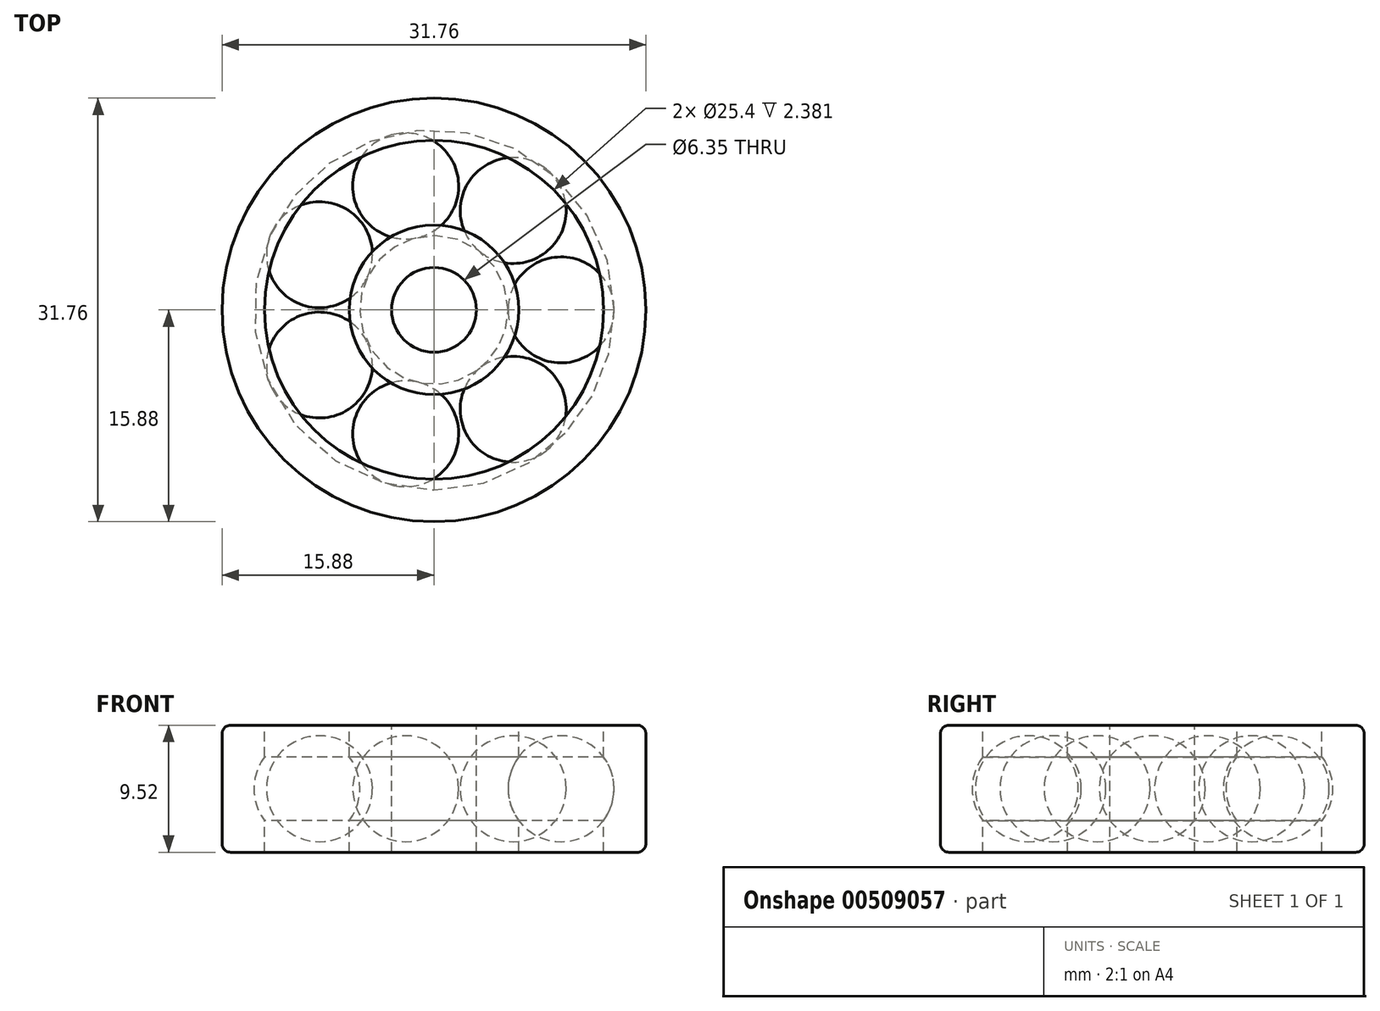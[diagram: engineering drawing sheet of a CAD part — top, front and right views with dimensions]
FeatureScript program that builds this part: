
annotation { "Feature Type Name" : "Feature", "Feature Type Description" : "" }
export const myFeature = defineFeature(function(context is Context, id is Id, definition is map)
    precondition{}
    {
        {
            var Q0;
            Q0=qCreatedBy(makeId("Front.planeOp"),FACE);
            var sketch = newSketch(context, id + "F0", { "sketchPlane" : qUnion([Q0])});
            skLineSegment(sketch, "E0", {"start": v(0, 19.05) * mm, "end": v(0, -19.05) * mm, "construction": true});
            skLineSegment(sketch, "E1", {"start": v(12.7, 19.05) * mm, "end": v(12.7, -19.05) * mm});
            skLineSegment(sketch, "E2", {"start": v(12.7, -19.05) * mm, "end": v(25.4, -19.05) * mm});
            skLineSegment(sketch, "E3", {"start": v(25.4, -19.05) * mm, "end": v(25.4, 19.05) * mm});
            skLineSegment(sketch, "E4", {"start": v(25.4, 19.05) * mm, "end": v(12.7, 19.05) * mm});
            skCircle(sketch, "E5", {"center": v(38.1, 0) * mm, "radius": 15.88 * mm});
            skLineSegment(sketch, "E6.bottom", {"start": v(50.8, 19.05) * mm, "end": v(63.5, 19.05) * mm});
            skLineSegment(sketch, "E6.top", {"start": v(50.8, -19.05) * mm, "end": v(63.5, -19.05) * mm});
            skLineSegment(sketch, "E6.left", {"start": v(50.8, 19.05) * mm, "end": v(50.8, -19.05) * mm});
            skLineSegment(sketch, "E6.right", {"start": v(63.5, 19.05) * mm, "end": v(63.5, -19.05) * mm});
            skLineSegment(sketch, "E7", {"start": v(22.22, 0) * mm, "end": v(53.97, 0) * mm});
            skLineSegment(sketch, "E8", {"start": v(12.7, 0) * mm, "end": v(22.22, 0) * mm, "construction": true});
            skLineSegment(sketch, "E9", {"start": v(53.97, 0) * mm, "end": v(63.5, 0) * mm, "construction": true});
            skSolve(sketch);
        }
        {
            var Q0;
            {var subQ0=sQuery(id+"F0.wireOp",EDGE,"E5");var subQ1=sQuery(id+"F0.wireOp",EDGE,"E3");var subQ2=makeQuery(id+"F0.imprint","INTERSECT",VERTEX,{"disambiguationData":[OD(1.0)],"derivedFrom":[subQ1,subQ0]});Q0=makeQuery(id+"F0.imprint","IMPRINT",FACE,{"disambiguationData":[TD([[makeQuery(id+"F0.imprint","IMPRINT",EDGE,{"disambiguationData":[TD([[subQ2,1.0]])],"derivedFrom":subQ1}),-1.0]])]});}
            var Q1;
            {var subQ0=sQuery(id+"F0.wireOp",EDGE,"E5");var subQ1=sQuery(id+"F0.wireOp",EDGE,"E3");var subQ2=makeQuery(id+"F0.imprint","INTERSECT",VERTEX,{"disambiguationData":[OD(1.0)],"derivedFrom":[subQ1,subQ0]});Q1=makeQuery(id+"F0.imprint","IMPRINT",FACE,{"disambiguationData":[TD([[makeQuery(id+"F0.imprint","IMPRINT",EDGE,{"disambiguationData":[TD([[subQ2,1.0]])],"derivedFrom":subQ1}),1.0]])]});}
            var Q2;
            {var subQ0=sQuery(id+"F0.wireOp",EDGE,"E7");var subQ1=sQuery(id+"F0.wireOp",EDGE,"E5");var subQ2=makeQuery(id+"F0.imprint","INTERSECT",VERTEX,{"disambiguationData":[OD(1.0)],"derivedFrom":[subQ1,subQ0]});Q2=makeQuery(id+"F0.imprint","IMPRINT",FACE,{"disambiguationData":[TD([[makeQuery(id+"F0.imprint","IMPRINT",EDGE,{"disambiguationData":[TD([[subQ2,-1.0]])],"derivedFrom":subQ1}),1.0]])]});}
            var Q3;
            Q3=sQuery(id+"F0.wireOp",EDGE,"E7");
            revolve(context, id + "F1", {"entities" : qUnion([Q0, Q1, Q2]), "axis" : qUnion([Q3]), "revolveType" : RevolveType.FULL});
        }
        {
            var Q0;
            Q0=makeQuery(id+"F0.imprint","IMPRINT",FACE,{"disambiguationData":[TD([[makeQuery(id+"F0.imprint","IMPRINT",EDGE,{"derivedFrom":sQuery(id+"F0.wireOp",EDGE,"E1")}),1.0]])]});
            var Q1;
            Q1=sQuery(id+"F0.wireOp",EDGE,"E0");
            revolve(context, id + "F2", {"entities" : qUnion([Q0]), "axis" : qUnion([Q1]), "revolveType" : RevolveType.FULL});
        }
        {
            var Q0;
            {var subQ1=sQuery(id+"F0.wireOp",EDGE,"E6.bottom");Q0=makeQuery(id+"F0.imprint","IMPRINT",FACE,{"disambiguationData":[TD([[makeQuery(id+"F0.imprint","IMPRINT",EDGE,{"derivedFrom":subQ1}),-1.0]])]});}
            var Q1;
            Q1=sQuery(id+"F0.wireOp",EDGE,"E0");
            revolve(context, id + "F3", {"entities" : qUnion([Q0]), "axis" : qUnion([Q1]), "revolveType" : RevolveType.FULL});
        }
        {
            var Q0;
            Q0=makeQuery(id+"F1.opRevolve","SWEPT_BODY",BODY,{"disambiguationData":[OSD([sQuery(id+"F0.wireOp",EDGE,"E5"),sQuery(id+"F0.wireOp",EDGE,"E7")])]});
            var Q1;
            Q1=sQuery(id+"F0.wireOp",EDGE,"E0");
            circularPattern(context, id + "F4", {"entities" : qUnion([Q0]), "axis" : qUnion([Q1]), "angle" : 360 * degree, "instanceCount" : 7, "equalSpace" : true, "computeTransformsWithoutBuiltin" : true});
        }
        {
            var Q0;
            Q0=makeQuery(id+"F3.opRevolve","SWEPT_EDGE",EDGE,{"disambiguationData":[OSD([sQuery(id+"F0.wireOp",EDGE,"E6.bottom"),sQuery(id+"F0.wireOp",EDGE,"E6.right")])]});
            var Q1;
            Q1=makeQuery(id+"F3.opRevolve","SWEPT_EDGE",EDGE,{"disambiguationData":[OSD([sQuery(id+"F0.wireOp",EDGE,"E6.top"),sQuery(id+"F0.wireOp",EDGE,"E6.right")])]});
            fillet(context, id + "F5", {"entities" : qUnion([Q0, Q1]), "radius" : 2.54 * mm, "tangentPropagation" : true, "allowEdgeOverflow" : false});
        }
        {
            var Q0;
            Q0=makeQuery(id+"F1.opRevolve","SWEPT_BODY",BODY,{"disambiguationData":[OSD([sQuery(id+"F0.wireOp",EDGE,"E5"),sQuery(id+"F0.wireOp",EDGE,"E7")])]});
            var Q1;
            Q1=makeQuery(id+"F2.opRevolve","SWEPT_BODY",BODY,{"disambiguationData":[OSD([sQuery(id+"F0.wireOp",EDGE,"E1"),sQuery(id+"F0.wireOp",EDGE,"E2"),sQuery(id+"F0.wireOp",EDGE,"E3"),sQuery(id+"F0.wireOp",EDGE,"E4"),sQuery(id+"F0.wireOp",EDGE,"E5")])]});
            var Q2;
            Q2=makeQuery(id+"F3.opRevolve","SWEPT_BODY",BODY,{"disambiguationData":[OSD([sQuery(id+"F0.wireOp",EDGE,"E5"),sQuery(id+"F0.wireOp",EDGE,"E6.bottom"),sQuery(id+"F0.wireOp",EDGE,"E6.top"),sQuery(id+"F0.wireOp",EDGE,"E6.left"),sQuery(id+"F0.wireOp",EDGE,"E6.right")])]});
            var Q3;
            Q3=makeQuery(id+"F4.opPattern","COPY",BODY,{"derivedFrom":makeQuery(id+"F1.opRevolve","SWEPT_BODY",BODY,{"disambiguationData":[OSD([sQuery(id+"F0.wireOp",EDGE,"E5"),sQuery(id+"F0.wireOp",EDGE,"E7")])]}),"instanceName":"1"});
            var Q4;
            Q4=makeQuery(id+"F4.opPattern","COPY",BODY,{"derivedFrom":makeQuery(id+"F1.opRevolve","SWEPT_BODY",BODY,{"disambiguationData":[OSD([sQuery(id+"F0.wireOp",EDGE,"E5"),sQuery(id+"F0.wireOp",EDGE,"E7")])]}),"instanceName":"2"});
            var Q5;
            Q5=makeQuery(id+"F4.opPattern","COPY",BODY,{"derivedFrom":makeQuery(id+"F1.opRevolve","SWEPT_BODY",BODY,{"disambiguationData":[OSD([sQuery(id+"F0.wireOp",EDGE,"E5"),sQuery(id+"F0.wireOp",EDGE,"E7")])]}),"instanceName":"3"});
            var Q6;
            Q6=makeQuery(id+"F4.opPattern","COPY",BODY,{"derivedFrom":makeQuery(id+"F1.opRevolve","SWEPT_BODY",BODY,{"disambiguationData":[OSD([sQuery(id+"F0.wireOp",EDGE,"E5"),sQuery(id+"F0.wireOp",EDGE,"E7")])]}),"instanceName":"4"});
            var Q7;
            Q7=makeQuery(id+"F4.opPattern","COPY",BODY,{"derivedFrom":makeQuery(id+"F1.opRevolve","SWEPT_BODY",BODY,{"disambiguationData":[OSD([sQuery(id+"F0.wireOp",EDGE,"E5"),sQuery(id+"F0.wireOp",EDGE,"E7")])]}),"instanceName":"5"});
            var Q8;
            Q8=makeQuery(id+"F4.opPattern","COPY",BODY,{"derivedFrom":makeQuery(id+"F1.opRevolve","SWEPT_BODY",BODY,{"disambiguationData":[OSD([sQuery(id+"F0.wireOp",EDGE,"E5"),sQuery(id+"F0.wireOp",EDGE,"E7")])]}),"instanceName":"6"});
            var Q9;
            Q9=qCreatedBy(makeId("Origin.pointOp"),VERTEX);
            transform(context, id + "F6", {"entities" : qUnion([Q0, Q1, Q2, Q3, Q4, Q5, Q6, Q7, Q8]), "transformType" : TransformType.SCALE_UNIFORMLY, "scale" : .25, "scalePoint" : qUnion([Q9]), "makeCopy" : false});
        }
    });
